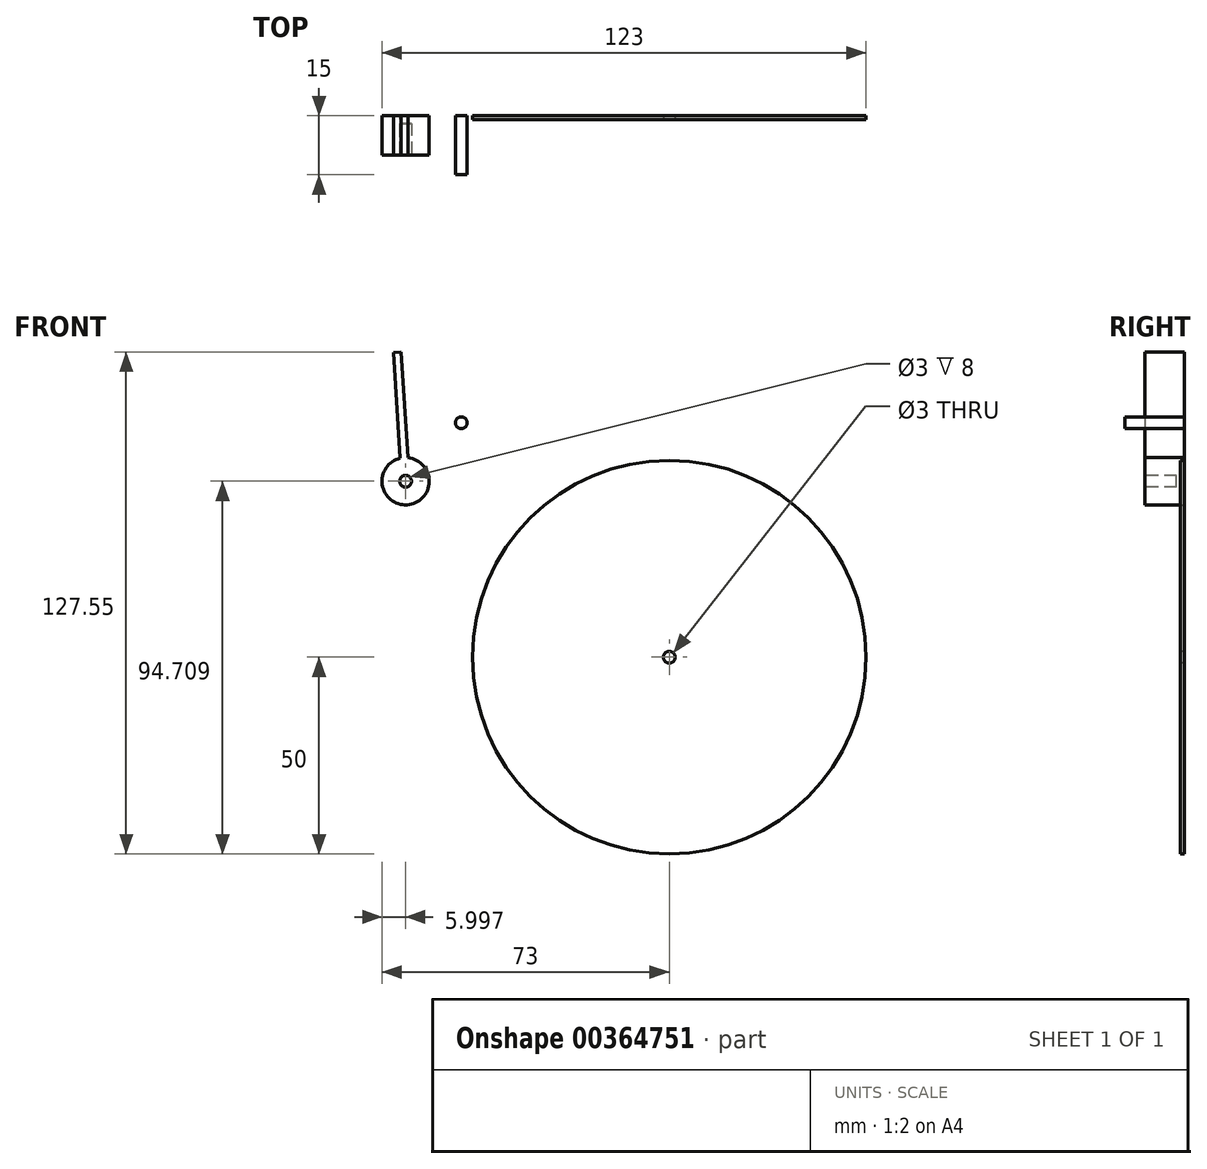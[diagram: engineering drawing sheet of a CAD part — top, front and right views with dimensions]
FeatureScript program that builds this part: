
annotation { "Feature Type Name" : "Feature", "Feature Type Description" : "" }
export const myFeature = defineFeature(function(context is Context, id is Id, definition is map)
    precondition{}
    {
        {
            var Q0;
            Q0=qCreatedBy(makeId("Front.planeOp"),FACE);
            var sketch = newSketch(context, id + "F0", { "sketchPlane" : qUnion([Q0])});
            skCircle(sketch, "E0", {"center": v(0, 0) * mm, "radius": 50 * mm});
            skSolve(sketch);
        }
        {
            var Q0;
            Q0=makeQuery(id+"F0.imprint","IMPRINT",FACE,{"disambiguationData":[TD([[makeQuery(id+"F0.imprint","IMPRINT",EDGE,{"derivedFrom":sQuery(id+"F0.wireOp",EDGE,"E0")}),1.0]])]});
            extrude(context, id + "F1", {"entities" : qUnion([Q0]), "depth" : 1 * mm});
        }
        {
            var Q0;
            Q0=qCreatedBy(makeId("Front.planeOp"),FACE);
            var sketch = newSketch(context, id + "F2", { "sketchPlane" : qUnion([Q0])});
            skCircle(sketch, "E1", {"center": v(0, 0) * mm, "radius": 1.5 * mm});
            skSolve(sketch);
        }
        {
            var Q0;
            Q0 = qSketchRegion(id + "F2", true);
            var Q1;
            Q1=makeQuery(id+"F1.opExtrude","CAP_FACE",FACE,{"disambiguationData":[OSD([sQuery(id+"F0.wireOp",EDGE,"E0")])],"isStart":false});
            extrude(context, id + "F3", {"entities" : qUnion([Q0]), "operationType" : NewBodyOperationType.REMOVE, "oppositeDirection" : true, "depth" : 25 * mm, "hasSecondDirection" : true, "secondDirectionBound" : SecondDirectionBoundingType.UP_TO_SURFACE, "secondDirectionOppositeDirection" : false, "secondDirectionBoundEntityFace" : qUnion([Q1]), "secondDirectionDepth" : 25 * mm});
        }
        {
            var Q0;
            Q0=qCreatedBy(makeId("Front.planeOp"),FACE);
            var sketch = newSketch(context, id + "F4", { "sketchPlane" : qUnion([Q0])});
            skCircle(sketch, "E2", {"center": v(-52.86, 59.57) * mm, "radius": 1.5 * mm});
            skSolve(sketch);
        }
        {
            var Q0;
            Q0=makeQuery(id+"F4.imprint","IMPRINT",FACE,{"disambiguationData":[TD([[makeQuery(id+"F4.imprint","IMPRINT",EDGE,{"derivedFrom":sQuery(id+"F4.wireOp",EDGE,"E2")}),1.0]])]});
            extrude(context, id + "F5", {"entities" : qUnion([Q0]), "depth" : 15 * mm});
        }
        {
            var Q0;
            Q0=qCreatedBy(makeId("Front.planeOp"),FACE);
            var sketch = newSketch(context, id + "F6", { "sketchPlane" : qUnion([Q0])});
            skCircle(sketch, "E3", {"center": v(-67, 44.7) * mm, "radius": 6 * mm});
            skSolve(sketch);
        }
        {
            var Q0;
            Q0=qCreatedBy(makeId("Front.planeOp"),FACE);
            cPlane(context, id + "F7", {"entities" : qUnion([Q0]), "cplaneType" : CPlaneType.OFFSET, "offset" : 2 * mm, "width" : 150 * mm, "height" : 150 * mm});
        }
        {
            var Q0;
            Q0=makeQuery(id+"F6.imprint","IMPRINT",FACE,{"disambiguationData":[TD([[makeQuery(id+"F6.imprint","IMPRINT",EDGE,{"derivedFrom":sQuery(id+"F6.wireOp",EDGE,"E3")}),1.0]])]});
            extrude(context, id + "F8", {"entities" : qUnion([Q0]), "depth" : 10 * mm});
        }
        {
            var Q0;
            Q0=makeQuery(id+"F8.opExtrude","CAP_FACE",FACE,{"disambiguationData":[OSD([sQuery(id+"F6.wireOp",EDGE,"E3")])],"isStart":false});
            var sketch = newSketch(context, id + "F9", { "sketchPlane" : qUnion([Q0])});
            skCircle(sketch, "E4", {"center": v(-67, 44.7) * mm, "radius": 1.5 * mm});
            skSolve(sketch);
        }
        {
            var Q0;
            Q0=makeQuery(id+"F9.imprint","IMPRINT",FACE,{"disambiguationData":[TD([[makeQuery(id+"F9.imprint","IMPRINT",EDGE,{"derivedFrom":sQuery(id+"F9.wireOp",EDGE,"E4")}),1.0]])]});
            var Q1;
            Q1=qCreatedBy(id+"F7.planeOp",FACE);
            extrude(context, id + "F10", {"entities" : qUnion([Q0]), "operationType" : NewBodyOperationType.REMOVE, "endBound" : BoundingType.UP_TO_SURFACE, "oppositeDirection" : true, "endBoundEntityFace" : qUnion([Q1]), "depth" : 25 * mm});
        }
        {
            var Q0;
            Q0=qCreatedBy(makeId("Front.planeOp"),FACE);
            var sketch = newSketch(context, id + "F11", { "sketchPlane" : qUnion([Q0])});
            skLineSegment(sketch, "E5", {"start": v(-67.38, 50.52) * mm, "end": v(-69.1, 77.5) * mm, "construction": true});
            skSolve(sketch);
        }
        {
            var Q0;
            Q0=qCreatedBy(makeId("Front.planeOp"),FACE);
            var sketch = newSketch(context, id + "F12", { "sketchPlane" : qUnion([Q0])});
            skLineSegment(sketch, "E6", {"start": v(-69.1, 77.5) * mm, "end": v(-70.1, 77.43) * mm});
            skLineSegment(sketch, "E7", {"start": v(-70.1, 77.43) * mm, "end": v(-68.38, 50.55) * mm});
            skLineSegment(sketch, "E8.MirrorCS", {"start": v(-68.1, 77.55) * mm, "end": v(-66.38, 50.68) * mm});
            skLineSegment(sketch, "E9.MirrorCS", {"start": v(-69.1, 77.5) * mm, "end": v(-68.1, 77.55) * mm});
            skLineSegment(sketch, "E10", {"start": v(-68.38, 50.55) * mm, "end": v(-66.38, 50.68) * mm});
            skSolve(sketch);
        }
        {
            var Q0;
            Q0=makeQuery(id+"F12.imprint","IMPRINT",FACE,{"disambiguationData":[TD([[makeQuery(id+"F12.imprint","IMPRINT",EDGE,{"derivedFrom":sQuery(id+"F12.wireOp",EDGE,"E6")}),1.0]])]});
            var Q1;
            Q1=makeQuery(id+"F8.opExtrude","CAP_FACE",FACE,{"disambiguationData":[OSD([sQuery(id+"F6.wireOp",EDGE,"E3")])],"isStart":false});
            extrude(context, id + "F13", {"entities" : qUnion([Q0]), "operationType" : NewBodyOperationType.ADD, "endBound" : BoundingType.UP_TO_SURFACE, "endBoundEntityFace" : qUnion([Q1]), "depth" : 25 * mm});
        }
    });
